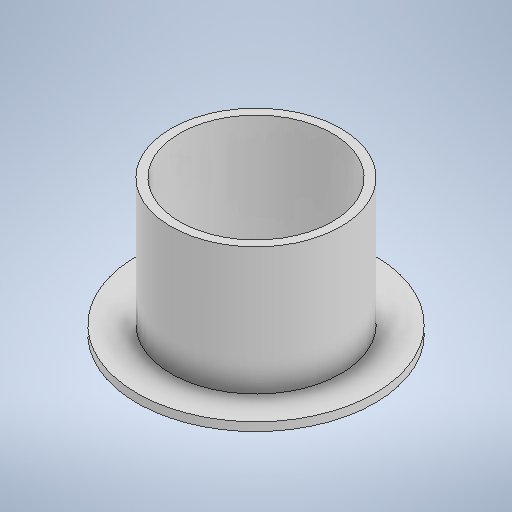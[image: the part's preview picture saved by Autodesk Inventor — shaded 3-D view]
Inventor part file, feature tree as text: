
AUTODESK INVENTOR PART (.ipt)
format: ipt  version: 2025 (Build 290162000, 162)  size: 255,488 bytes
history: native  units: mm
features: sketch x7, extrude x4, other x1
ambient origin geometry x8: Origin, YZ Plane, XZ Plane, XY Plane, X Axis, Y Axis, Z Axis, Center Point
bodies: Body1 (feature_tree)
feature tree (12):
  other  "Bryła1"
  extrude  "Wyciągnięcie proste1"  Depth=100.0mm
  extrude  "Wyciągnięcie proste2"  Depth=80.0mm TaperAngle=0.0deg
  sketch  "Szkic3"
  extrude  "Wyciągnięcie proste3"  Depth=90.0mm
  sketch  "Szkic9"
  extrude  "Wyciągnięcie proste4"  Depth=75.0mm TaperAngle=0.0deg
  sketch  "Szkic11"
  sketch  "Szkic1"
  sketch  "Szkic2"
  sketch  "Szkic4"
  sketch  "Szkic10"
